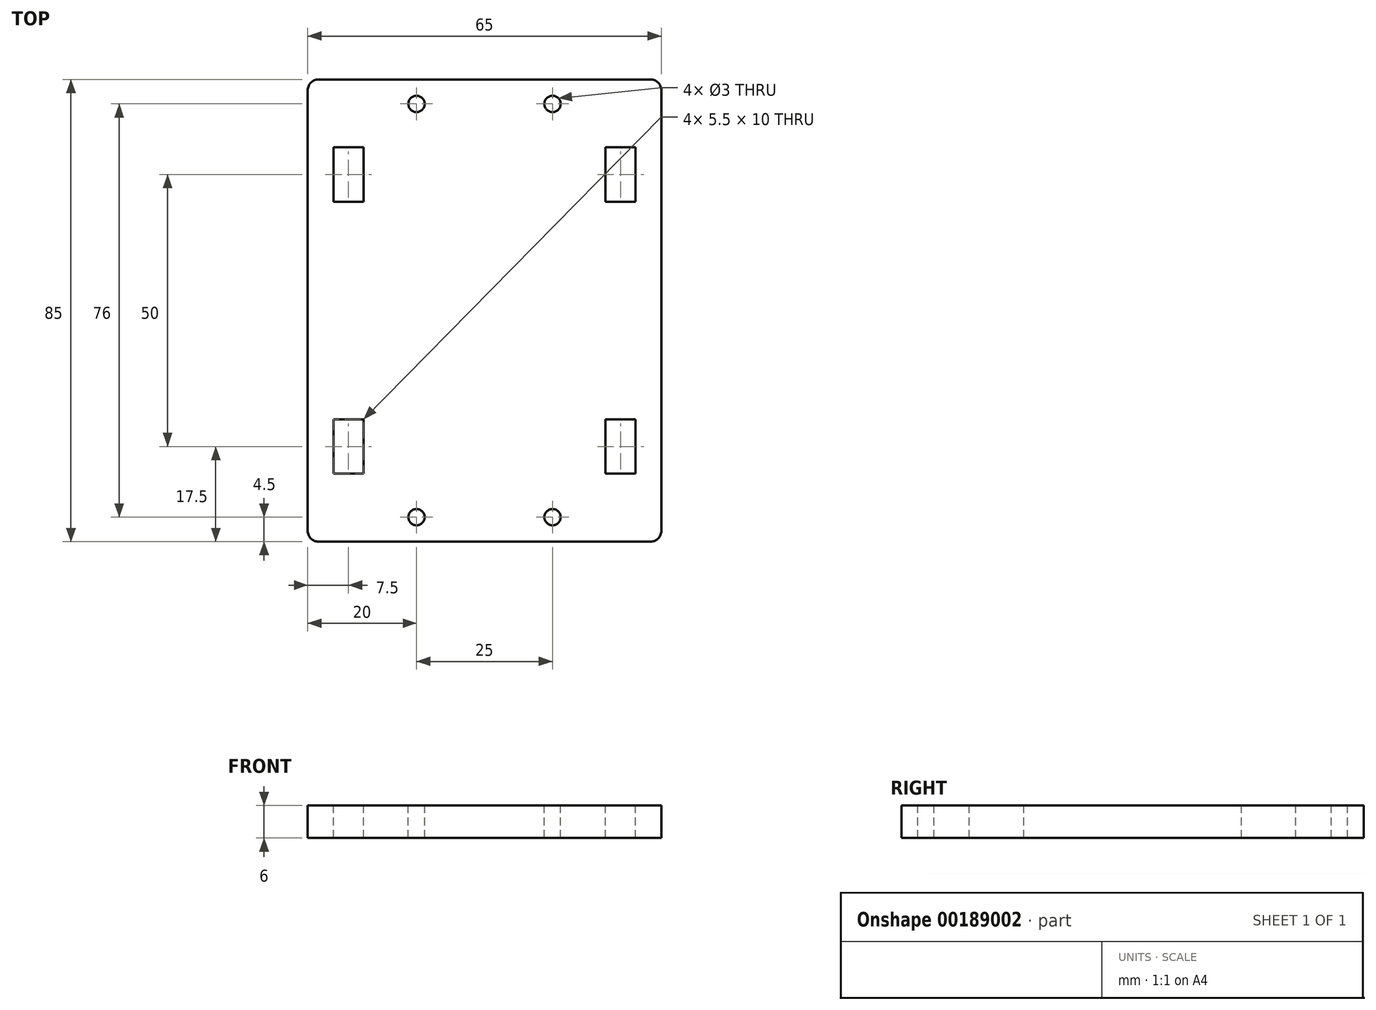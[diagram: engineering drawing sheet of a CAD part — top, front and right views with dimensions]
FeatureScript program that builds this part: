
annotation { "Feature Type Name" : "Feature", "Feature Type Description" : "" }
export const myFeature = defineFeature(function(context is Context, id is Id, definition is map)
    precondition{}
    {
        {
            var Q0;
            Q0=qCreatedBy(makeId("Top.planeOp"),FACE);
            var sketch = newSketch(context, id + "F0", { "sketchPlane" : qUnion([Q0])});
            skLineSegment(sketch, "E0.bottom", {"start": v(30.5, -42.5) * mm, "end": v(-30.5, -42.5) * mm});
            skLineSegment(sketch, "E0.top", {"start": v(30.5, 42.5) * mm, "end": v(-30.5, 42.5) * mm});
            skLineSegment(sketch, "E0.left", {"start": v(32.5, -40.5) * mm, "end": v(32.5, 40.5) * mm});
            skLineSegment(sketch, "E0.right", {"start": v(-32.5, -40.5) * mm, "end": v(-32.5, 40.5) * mm});
            skPoint(sketch, "E0.middle", {"position": v(0, 0) * mm});
            skPoint(sketch, "E1.visualSharp", {"position": v(-32.5, 42.5) * mm});
            skArc(sketch, "E1.filletArc", {"start": v(-30.5, 42.5) * mm, "mid": v(-31.91, 41.91) * mm, "end": v(-32.5, 40.5) * mm});
            skPoint(sketch, "E2.visualSharp", {"position": v(32.5, 42.5) * mm});
            skArc(sketch, "E2.filletArc", {"start": v(32.5, 40.5) * mm, "mid": v(31.91, 41.91) * mm, "end": v(30.5, 42.5) * mm});
            skPoint(sketch, "E3.visualSharp", {"position": v(32.5, -42.5) * mm});
            skArc(sketch, "E3.filletArc", {"start": v(30.5, -42.5) * mm, "mid": v(31.91, -41.91) * mm, "end": v(32.5, -40.5) * mm});
            skPoint(sketch, "E4.visualSharp", {"position": v(-32.5, -42.5) * mm});
            skArc(sketch, "E4.filletArc", {"start": v(-32.5, -40.5) * mm, "mid": v(-31.91, -41.91) * mm, "end": v(-30.5, -42.5) * mm});
            skSolve(sketch);
        }
        {
            var Q0;
            Q0 = qSketchRegion(id + "F0", true);
            extrude(context, id + "F1", {"entities" : qUnion([Q0]), "depth" : 6 * mm});
        }
        {
            var Q0;
            Q0=makeQuery(id+"F1.opExtrude","CAP_FACE",FACE,{"disambiguationData":[OSD([sQuery(id+"F0.wireOp",EDGE,"E0.bottom"),sQuery(id+"F0.wireOp",EDGE,"E0.top"),sQuery(id+"F0.wireOp",EDGE,"E0.left"),sQuery(id+"F0.wireOp",EDGE,"E0.right"),sQuery(id+"F0.wireOp",EDGE,"E1.filletArc"),sQuery(id+"F0.wireOp",EDGE,"E2.filletArc"),sQuery(id+"F0.wireOp",EDGE,"E3.filletArc"),sQuery(id+"F0.wireOp",EDGE,"E4.filletArc")])],"isStart":false});
            var sketch = newSketch(context, id + "F2", { "sketchPlane" : qUnion([Q0])});
            skLineSegment(sketch, "E5.bottom", {"start": v(-22.25, 20) * mm, "end": v(-27.75, 20) * mm});
            skLineSegment(sketch, "E5.top", {"start": v(-22.25, 30) * mm, "end": v(-27.75, 30) * mm});
            skLineSegment(sketch, "E5.left", {"start": v(-22.25, 20) * mm, "end": v(-22.25, 30) * mm});
            skLineSegment(sketch, "E5.right", {"start": v(-27.75, 20) * mm, "end": v(-27.75, 30) * mm});
            skPoint(sketch, "E5.middle", {"position": v(-25, 25) * mm});
            skLineSegment(sketch, "E6.bottom", {"start": v(27.75, 20) * mm, "end": v(22.25, 20) * mm});
            skLineSegment(sketch, "E6.top", {"start": v(27.75, 30) * mm, "end": v(22.25, 30) * mm});
            skLineSegment(sketch, "E6.left", {"start": v(27.75, 20) * mm, "end": v(27.75, 30) * mm});
            skLineSegment(sketch, "E6.right", {"start": v(22.25, 20) * mm, "end": v(22.25, 30) * mm});
            skPoint(sketch, "E6.middle", {"position": v(25, 25) * mm});
            skLineSegment(sketch, "E7.bottom", {"start": v(27.75, -30) * mm, "end": v(22.25, -30) * mm});
            skLineSegment(sketch, "E7.top", {"start": v(27.75, -20) * mm, "end": v(22.25, -20) * mm});
            skLineSegment(sketch, "E7.left", {"start": v(27.75, -30) * mm, "end": v(27.75, -20) * mm});
            skLineSegment(sketch, "E7.right", {"start": v(22.25, -30) * mm, "end": v(22.25, -20) * mm});
            skPoint(sketch, "E7.middle", {"position": v(25, -25) * mm});
            skLineSegment(sketch, "E8.bottom", {"start": v(-22.25, -30) * mm, "end": v(-27.75, -30) * mm});
            skLineSegment(sketch, "E8.top", {"start": v(-22.25, -20) * mm, "end": v(-27.75, -20) * mm});
            skLineSegment(sketch, "E8.left", {"start": v(-22.25, -30) * mm, "end": v(-22.25, -20) * mm});
            skLineSegment(sketch, "E8.right", {"start": v(-27.75, -30) * mm, "end": v(-27.75, -20) * mm});
            skPoint(sketch, "E8.middle", {"position": v(-25, -25) * mm});
            skLineSegment(sketch, "E9.bottom", {"start": v(25, -25) * mm, "end": v(-25, -25) * mm, "construction": true});
            skLineSegment(sketch, "E9.top", {"start": v(25, 25) * mm, "end": v(-25, 25) * mm, "construction": true});
            skLineSegment(sketch, "E9.left", {"start": v(25, -25) * mm, "end": v(25, 25) * mm, "construction": true});
            skLineSegment(sketch, "E9.right", {"start": v(-25, -25) * mm, "end": v(-25, 25) * mm, "construction": true});
            skPoint(sketch, "E9.middle", {"position": v(0, 0) * mm});
            skSolve(sketch);
        }
        {
            var Q0;
            Q0 = qSketchRegion(id + "F2", true);
            extrude(context, id + "F3", {"entities" : qUnion([Q0]), "operationType" : NewBodyOperationType.REMOVE, "oppositeDirection" : true, "depth" : 25 * mm});
        }
        {
            var Q0;
            Q0=makeQuery(id+"F1.opExtrude","CAP_FACE",FACE,{"disambiguationData":[OSD([sQuery(id+"F0.wireOp",EDGE,"E0.bottom"),sQuery(id+"F0.wireOp",EDGE,"E0.top"),sQuery(id+"F0.wireOp",EDGE,"E0.left"),sQuery(id+"F0.wireOp",EDGE,"E0.right"),sQuery(id+"F0.wireOp",EDGE,"E1.filletArc"),sQuery(id+"F0.wireOp",EDGE,"E2.filletArc"),sQuery(id+"F0.wireOp",EDGE,"E3.filletArc"),sQuery(id+"F0.wireOp",EDGE,"E4.filletArc")])],"isStart":false});
            var sketch = newSketch(context, id + "F4", { "sketchPlane" : qUnion([Q0])});
            skLineSegment(sketch, "E10.bottom", {"start": v(12.5, -38) * mm, "end": v(-12.5, -38) * mm, "construction": true});
            skLineSegment(sketch, "E10.top", {"start": v(12.5, 38) * mm, "end": v(-12.5, 38) * mm, "construction": true});
            skLineSegment(sketch, "E10.left", {"start": v(12.5, -38) * mm, "end": v(12.5, 38) * mm, "construction": true});
            skLineSegment(sketch, "E10.right", {"start": v(-12.5, -38) * mm, "end": v(-12.5, 38) * mm, "construction": true});
            skPoint(sketch, "E10.middle", {"position": v(0, 0) * mm});
            skCircle(sketch, "E11", {"center": v(-12.5, 38) * mm, "radius": 1.5 * mm});
            skCircle(sketch, "E12", {"center": v(12.5, 38) * mm, "radius": 1.5 * mm});
            skCircle(sketch, "E13", {"center": v(12.5, -38) * mm, "radius": 1.5 * mm});
            skCircle(sketch, "E14", {"center": v(-12.5, -38) * mm, "radius": 1.5 * mm});
            skSolve(sketch);
        }
        {
            var Q0;
            Q0 = qSketchRegion(id + "F4", true);
            extrude(context, id + "F5", {"entities" : qUnion([Q0]), "operationType" : NewBodyOperationType.REMOVE, "oppositeDirection" : true, "depth" : 6 * mm});
        }
    });
